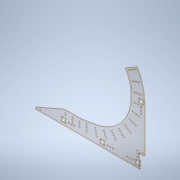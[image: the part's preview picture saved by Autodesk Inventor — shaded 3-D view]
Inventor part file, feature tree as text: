
AUTODESK INVENTOR PART (.ipt)
format: ipt  version: 2020 (Build 240168000, 168)  size: 496,128 bytes
history: native  units: in
note: dims shown in document units (in); Inventor stores cm internally (conversion verified against a paired STEP export)
features: extrude x4, sketch x4, fillet x1
ambient origin geometry x8: Origin, YZ Plane, XZ Plane, XY Plane, X Axis, Y Axis, Z Axis, Center Point
bodies: Solid1 (feature_tree)
feature tree (9):
  extrude  "Extrusion1"  Depth=0.25in
  extrude  "Extrusion2"  Depth=0.25in TaperAngle=0.0deg
  extrude  "Extrusion3"  TaperAngle=0.0deg  [1 undecoded]
  fillet  "Fillet1"  Radius=0.125in
  extrude  "Extrusion4"  Depth=0.5in
  sketch  "Sketch1"  dims[d0=0.25in d1=0.0in d2=0.25in]
  sketch  "Sketch2"  dims[d3=0.5in d4=0.25in d5=0.0in]
  sketch  "Sketch3"  dims[d6=0.3in d7=0.0in d8=0.0in d9=0.125in]
  sketch  "Sketch4"  dims[d10=0.2031in d11=0.5in d12=2.0in d13=0.5in d14=0.5in d15=0.5in d16=0.5in d17=13.134in d18=0.5in d19=0.5in d20=4.7244in d22=120.0deg d24=1.5748in d26=2.0in d27=0.3937in d29=1.0in d31=1.0in d32=0.0in]
note: 1 required parameter value undecoded (feature->parameter linkage not recoverable at this tier; creation-order binding heuristic only, values carry confidence <= 0.55)
